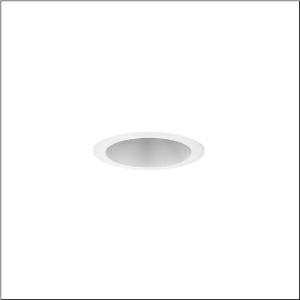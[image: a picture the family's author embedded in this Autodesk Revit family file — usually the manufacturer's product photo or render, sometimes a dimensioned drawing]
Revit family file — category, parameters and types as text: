
# Revit family: lunis_31_mini_51dn16de41
name_source: partatom
category: Lighting Fixtures
units: mm (PartAtom-declared; Revit-internal decimal feet)

## family parameters
Cut with Voids When Loaded = No
Host = Face
Light Source = No
Part Type = Normal
Room Calculation Point = No
Round Connector Dimension = Use Diameter
Shared = No

## types (1)
- Lunis 31 mini (1 x LED, 1040 lm, 8.3 W, 4000K)
    Apparent Load = 8 VA
    CIE Flux Codes = 69 93 99 100 100
    Color Rendering = 80
    Color Temperature = 4000K
    Default Elevation = 1800 mm
    Description = Lunis 31,  mini, downlight, light control with reflector, light emission: direct distribution, LED rated luminous flux: 1.040lm, light colour: 840, control gear: ECG DALI, mains connection: 220..240V, AC, 50/60Hz, housing, white, protection rating (complete): IP20, protection rating (on room side): IP54, insulation class (complete): insulation class II (safety insulation), certification: CE, packaging unit: 1 piece
    Height = 0 mm  [stored 0 ft]
    Lamp = 1 x LED
    Lamp Light Flux = 1040 lm
    Lamp Power = 8.3 W
    Lamp count = 1
    Length = 188 mm  [stored 0.616798 ft]
    Luminous efficacy = 125 lm/W
    Manufacturer = Siteco
    ModVariant = No
    Model = 51DN16DE41
    Mounting Place = Ceiling
    Mounting Type = Recessed
    Number of Poles = 1
    OnlyDefault = Yes
    Power Factor = 1
    Product Name = Lunis 31 mini
    Product group = downlight
    ProductGroupID = 400
    Protection Class = Protection class II
    Protection Degree = IP 20
    RLX_Detail_Level = 1
    RLX_Emergency_Light_Flux = 0 lm
    RLX_Emergency_Type = 0
    RLX_Emergency_Type_DB = No
    RlxData = <blob elided: 21777 chars, md5=2c3c3bb9>
    Socket = socket
    Standby Power = 0 W
    System Light Flux = 1040 lm
    System Power = 8 W
    Type Comments = Product without accessories
    Type Image = l_1005624.jpg
    URL = http://relux.com
    VarID = ---
    Voltage = 0 V
    Weight = 0.00 kg
    Width = 0 mm  [stored 0 ft]

note: [stored X ft] marks values corroborated as IEEE doubles in the binary element streams (Revit-internal decimal feet)

## geometry (parser evidence)
native form markers: Blend x4, Sweep x11
no freeform markers — native parametric forms only
